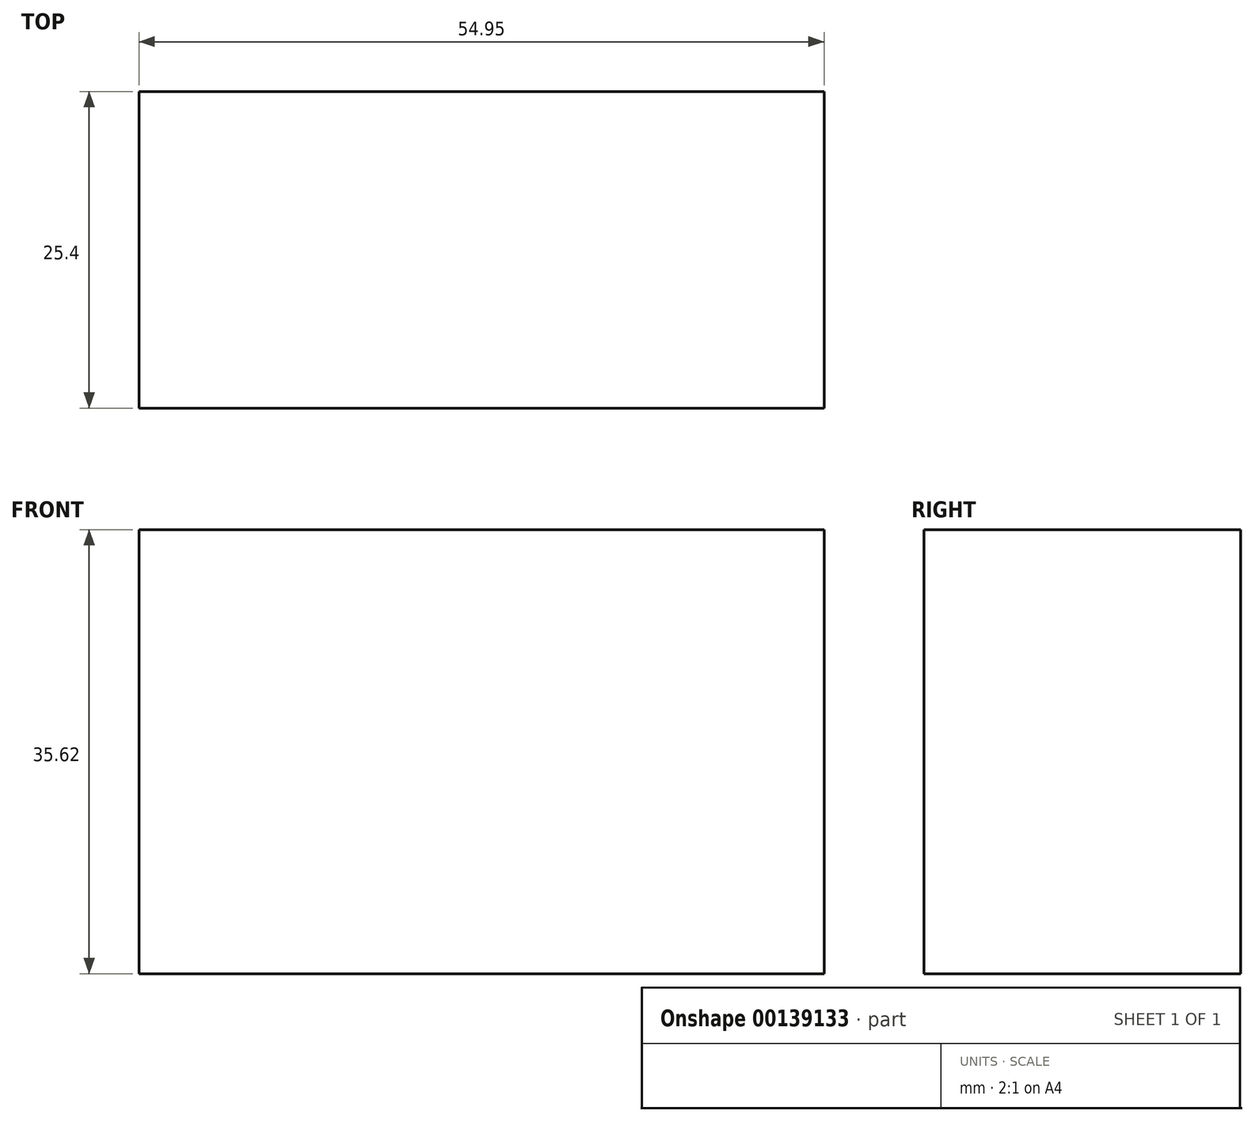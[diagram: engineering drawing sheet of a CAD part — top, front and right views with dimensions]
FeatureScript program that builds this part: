
annotation { "Feature Type Name" : "Feature", "Feature Type Description" : "" }
export const myFeature = defineFeature(function(context is Context, id is Id, definition is map)
    precondition{}
    {
        {
            var Q0;
            Q0=qCreatedBy(makeId("Front.planeOp"),FACE);
            var sketch = newSketch(context, id + "F0", { "sketchPlane" : qUnion([Q0])});
            skLineSegment(sketch, "E0.bottom", {"start": v(-33.96, 13.09) * mm, "end": v(20.99, 13.09) * mm});
            skLineSegment(sketch, "E0.top", {"start": v(-33.96, -22.53) * mm, "end": v(20.99, -22.53) * mm});
            skLineSegment(sketch, "E0.left", {"start": v(-33.96, 13.09) * mm, "end": v(-33.96, -22.53) * mm});
            skLineSegment(sketch, "E0.right", {"start": v(20.99, 13.09) * mm, "end": v(20.99, -22.53) * mm});
            skSolve(sketch);
        }
        {
            var Q0;
            Q0=makeQuery(id+"F0.imprint","IMPRINT",FACE,{"disambiguationData":[TD([[makeQuery(id+"F0.imprint","IMPRINT",EDGE,{"derivedFrom":sQuery(id+"F0.wireOp",EDGE,"E0.bottom")}),-1.0]])]});
            extrude(context, id + "F1", {"entities" : qUnion([Q0]), "depth" : 25.4 * mm});
        }
    });
